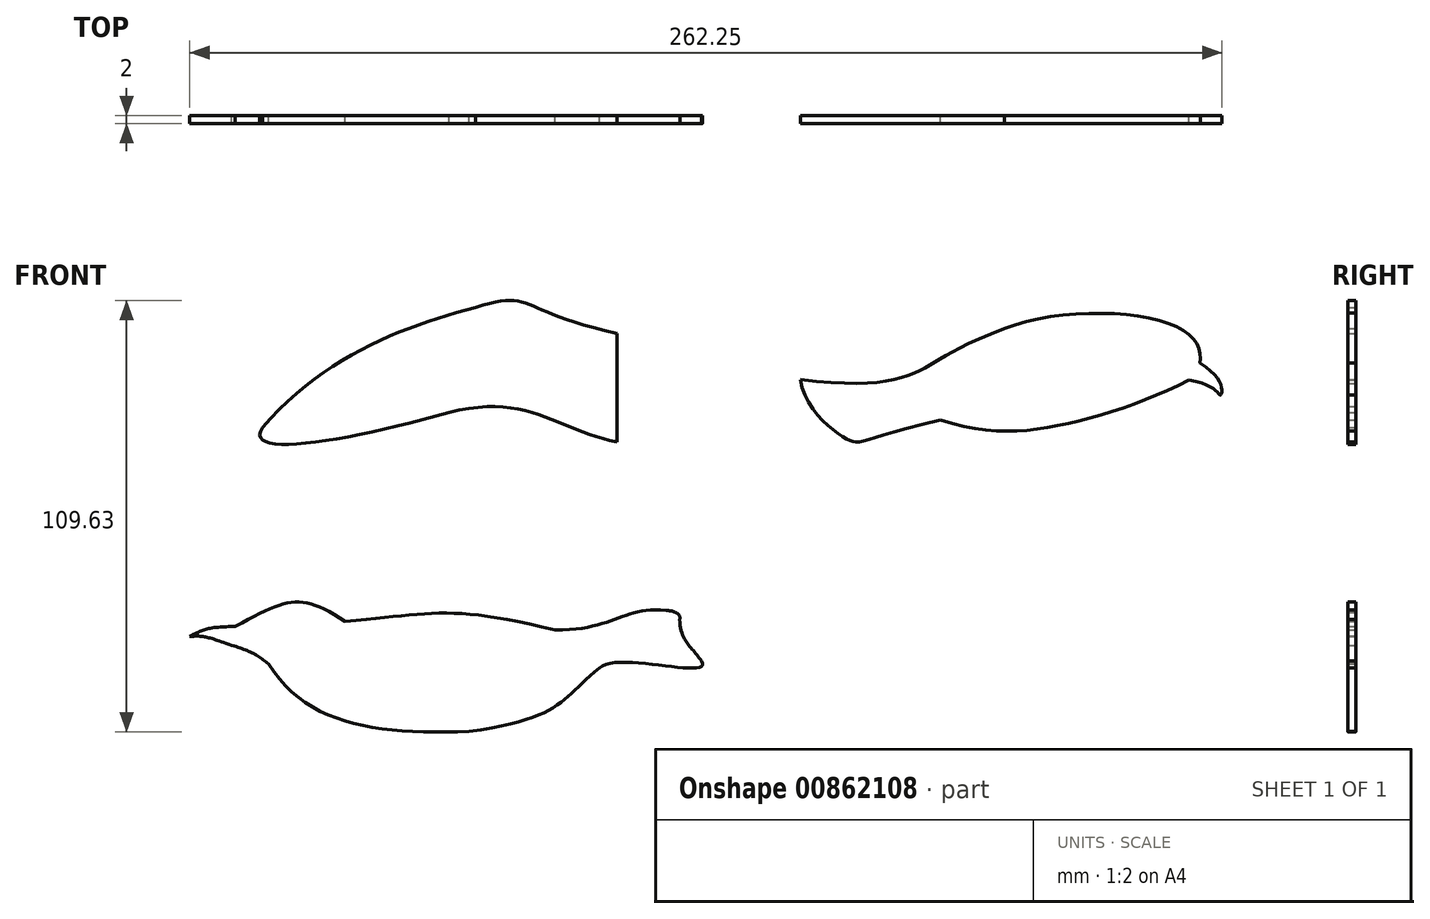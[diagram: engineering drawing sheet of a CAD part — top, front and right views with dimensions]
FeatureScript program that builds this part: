
annotation { "Feature Type Name" : "Feature", "Feature Type Description" : "" }
export const myFeature = defineFeature(function(context is Context, id is Id, definition is map)
    precondition{}
    {
        {
            var Q0;
            Q0=qCreatedBy(makeId("Front.planeOp"),FACE);
            var sketch = newSketch(context, id + "F0", { "sketchPlane" : qUnion([Q0])});
            skFitSpline(sketch, "E0", {"points": [v(54.41, 62.6) * mm, v(84.23, 61.14) * mm, v(117.5, 72.7) * mm], "startDerivative": vector(71.89, -23.28) * mm, "endDerivative": vector(60.93, 31.35) * mm});
            skFitSpline(sketch, "E1", {"points": [v(117.5, 72.7) * mm, v(125.58, 68.9) * mm, v(120.27, 77.03) * mm], "startDerivative": vector(45.01, -7.1) * mm, "endDerivative": vector(-38.76, 22.6) * mm});
            skFitSpline(sketch, "E2", {"points": [v(120.27, 77.03) * mm, v(115.59, 85.7) * mm, v(70.67, 85.8) * mm], "startDerivative": vector(5.65, 27.55) * mm, "endDerivative": vector(-58.66, -24.17) * mm});
            skFitSpline(sketch, "E3", {"points": [v(70.67, 85.8) * mm, v(49.49, 75.28) * mm, v(18.82, 72.9) * mm], "startDerivative": vector(-86.85, -32.49) * mm, "endDerivative": vector(-97.66, 12.93) * mm});
            skFitSpline(sketch, "E4", {"points": [v(18.82, 72.9) * mm, v(30.26, 57.93) * mm, v(54.41, 62.6) * mm], "startDerivative": vector(6.8, -48.33) * mm, "endDerivative": vector(117.25, 27.57) * mm});
            skFitSpline(sketch, "E5", {"points": [v(-27.81, 84.61) * mm, v(-63.74, 91.19) * mm], "startDerivative": vector(-76.01, 16.41) * mm, "endDerivative": vector(-45.74, -14.27) * mm});
            skFitSpline(sketch, "E6", {"points": [v(-63.74, 91.19) * mm, v(-117.81, 60.63) * mm], "startDerivative": vector(-54.28, -14.6) * mm, "endDerivative": vector(-47.45, -55.62) * mm});
            skFitSpline(sketch, "E7", {"points": [v(-117.81, 60.63) * mm, v(-70.41, 64.48) * mm], "startDerivative": vector(-16.57, -24.21) * mm, "endDerivative": vector(75.7, 21.58) * mm});
            skLineSegment(sketch, "E8", {"start": v(49.77, 82.68) * mm, "end": v(87.74, 94.58) * mm, "construction": true});
            skLineSegment(sketch, "E9", {"start": v(-117.81, 56.26) * mm, "end": v(-7.81, 56.26) * mm, "construction": true});
            skLineSegment(sketch, "E10", {"start": v(-117.81, 94.84) * mm, "end": v(-7.81, 94.84) * mm, "construction": true});
            skLineSegment(sketch, "E11", {"start": v(-27.81, 111.08) * mm, "end": v(-27.81, 46.97) * mm, "construction": true});
            skLineSegment(sketch, "E12", {"start": v(-27.81, 84.61) * mm, "end": v(-27.81, 57.04) * mm});
            skFitSpline(sketch, "E13", {"points": [v(-70.41, 64.48) * mm, v(-27.81, 57.04) * mm], "startDerivative": vector(60.76, 15.8) * mm, "endDerivative": vector(42.6, -7.45) * mm});
            skFitSpline(sketch, "E14", {"points": [v(-136.34, 7.56) * mm, v(-124.79, 10.13) * mm], "startDerivative": vector(10.75, 5.82) * mm, "endDerivative": vector(20.11, 0.38) * mm});
            skFitSpline(sketch, "E15", {"points": [v(-124.79, 10.13) * mm, v(-96.86, 11.4) * mm], "startDerivative": vector(40.88, 21.85) * mm, "endDerivative": vector(34.44, -22.56) * mm});
            skFitSpline(sketch, "E16", {"points": [v(-96.86, 11.4) * mm, v(-43.51, 9.2) * mm], "startDerivative": vector(65.88, 5.72) * mm, "endDerivative": vector(80.85, -20.07) * mm});
            skFitSpline(sketch, "E17", {"points": [v(-43.51, 9.2) * mm, v(-15.37, 14.25) * mm], "startDerivative": vector(45.13, 0.08) * mm, "endDerivative": vector(32.76, -2.78) * mm});
            skFitSpline(sketch, "E18", {"points": [v(-15.37, 14.25) * mm, v(-11.87, 11.93) * mm], "startDerivative": vector(8.22, -0.76) * mm, "endDerivative": vector(-1.14, -3.8) * mm});
            skFitSpline(sketch, "E19", {"points": [v(-11.87, 11.93) * mm, v(-6.34, 1.34) * mm], "startDerivative": vector(1.04, -18.75) * mm, "endDerivative": vector(6.09, -10.28) * mm});
            skFitSpline(sketch, "E20", {"points": [v(-6.34, 1.34) * mm, v(-32.17, -0.36) * mm], "startDerivative": vector(10.61, -15.16) * mm, "endDerivative": vector(-12.68, -13) * mm});
            skFitSpline(sketch, "E21", {"points": [v(-32.17, -0.36) * mm, v(-65.31, -16.57) * mm], "startDerivative": vector(-30.39, -24.36) * mm, "endDerivative": vector(-72.59, -10.6) * mm});
            skFitSpline(sketch, "E22", {"points": [v(-65.31, -16.57) * mm, v(-116.3, 0.56) * mm], "startDerivative": vector(-69.72, -2.21) * mm, "endDerivative": vector(-29.78, 47.38) * mm});
            skFitSpline(sketch, "E23", {"points": [v(-116.3, 0.56) * mm, v(-125.65, 5.3) * mm], "startDerivative": vector(-7.75, 7) * mm, "endDerivative": vector(-12.79, 3.6) * mm});
            skFitSpline(sketch, "E24", {"points": [v(-136.34, 7.56) * mm, v(-125.65, 5.3) * mm], "startDerivative": vector(11.9, 1.21) * mm, "endDerivative": vector(17.4, -5.9) * mm});
            skLineSegment(sketch, "E25", {"start": v(-71.84, 13.52) * mm, "end": v(-71.84, -16.7) * mm, "construction": true});
            skSolve(sketch);
        }
        {
            var Q0;
            Q0=makeQuery(id+"F0.imprint","IMPRINT",FACE,{"disambiguationData":[TD([[makeQuery(id+"F0.imprint","IMPRINT",EDGE,{"derivedFrom":sQuery(id+"F0.wireOp",EDGE,"E0")}),1.0]])]});
            extrude(context, id + "F1", {"entities" : qUnion([Q0]), "depth" : 2 * mm, "offsetDistance" : 25 * mm});
        }
        {
            var Q0;
            Q0=makeQuery(id+"F0.imprint","IMPRINT",FACE,{"disambiguationData":[TD([[makeQuery(id+"F0.imprint","IMPRINT",EDGE,{"derivedFrom":sQuery(id+"F0.wireOp",EDGE,"E5")}),1.0]])]});
            extrude(context, id + "F2", {"entities" : qUnion([Q0]), "depth" : 2 * mm, "offsetDistance" : 25 * mm});
        }
        {
            var Q0;
            Q0=makeQuery(id+"F0.imprint","IMPRINT",FACE,{"disambiguationData":[TD([[makeQuery(id+"F0.imprint","IMPRINT",EDGE,{"derivedFrom":sQuery(id+"F0.wireOp",EDGE,"E14")}),-1.0]])]});
            extrude(context, id + "F3", {"entities" : qUnion([Q0]), "depth" : 2 * mm, "offsetDistance" : 25 * mm});
        }
    });
